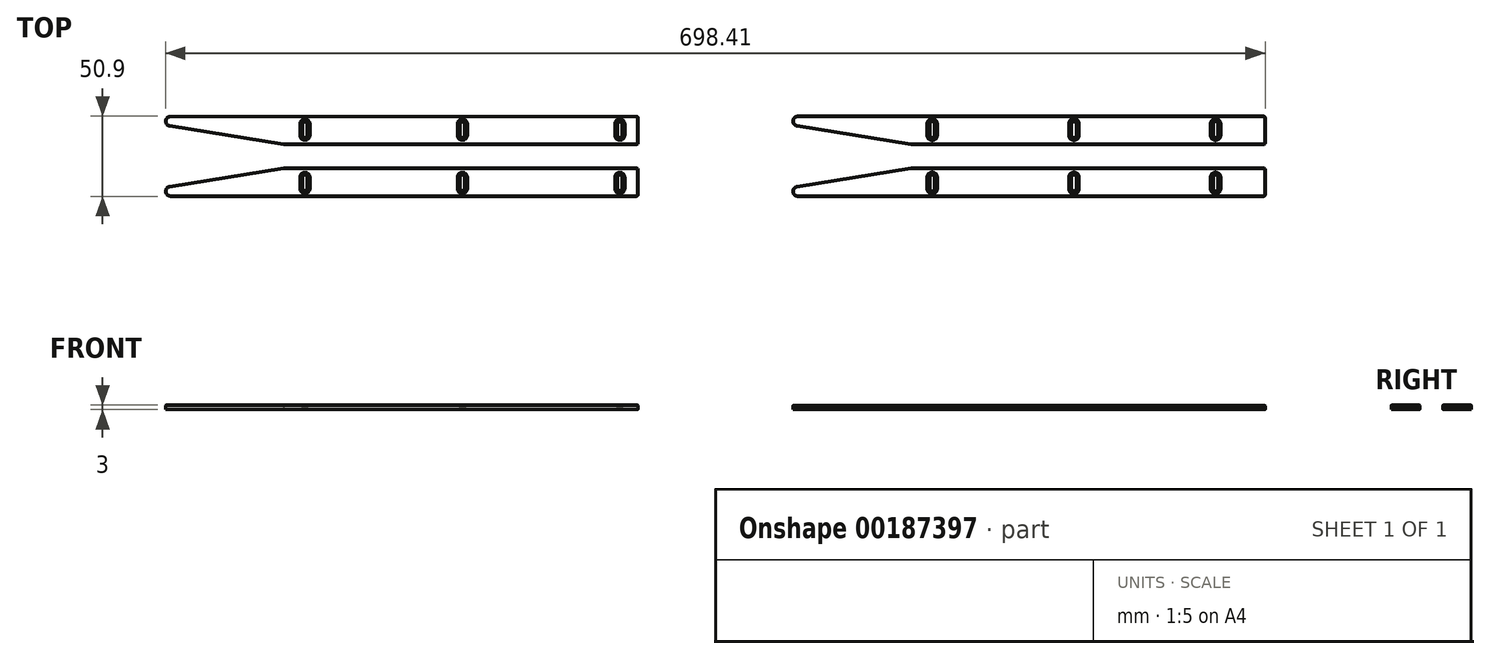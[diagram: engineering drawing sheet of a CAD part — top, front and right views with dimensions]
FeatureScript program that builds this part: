
annotation { "Feature Type Name" : "Feature", "Feature Type Description" : "" }
export const myFeature = defineFeature(function(context is Context, id is Id, definition is map)
    precondition{}
    {
        {
            var Q0;
            Q0=qCreatedBy(makeId("Top.planeOp"),FACE);
            var sketch = newSketch(context, id + "F0", { "sketchPlane" : qUnion([Q0])});
            skLineSegment(sketch, "E0.bottom", {"start": v(0, 0) * mm, "end": v(300, 0) * mm});
            skLineSegment(sketch, "E0.top", {"start": v(0, 18) * mm, "end": v(300, 18) * mm});
            skLineSegment(sketch, "E0.left", {"start": v(0, 0) * mm, "end": v(0, 18) * mm});
            skLineSegment(sketch, "E0.right", {"start": v(300, 0) * mm, "end": v(300, 18) * mm});
            skLineSegment(sketch, "E1.bottom", {"start": v(89.97, 5) * mm, "end": v(86.97, 5) * mm});
            skLineSegment(sketch, "E1.top", {"start": v(89.97, 12) * mm, "end": v(86.97, 12) * mm});
            skLineSegment(sketch, "E1.left", {"start": v(89.97, 5) * mm, "end": v(89.97, 12) * mm});
            skLineSegment(sketch, "E1.right", {"start": v(86.97, 5) * mm, "end": v(86.97, 12) * mm});
            skPoint(sketch, "E1.middle", {"position": v(88.47, 8.5) * mm});
            skLineSegment(sketch, "E2.bottom", {"start": v(189.97, 5) * mm, "end": v(186.97, 5) * mm});
            skLineSegment(sketch, "E2.top", {"start": v(189.97, 12) * mm, "end": v(186.97, 12) * mm});
            skLineSegment(sketch, "E2.left", {"start": v(189.97, 5) * mm, "end": v(189.97, 12) * mm});
            skLineSegment(sketch, "E2.right", {"start": v(186.97, 5) * mm, "end": v(186.97, 12) * mm});
            skPoint(sketch, "E2.middle", {"position": v(188.47, 8.5) * mm});
            skArc(sketch, "E3", {"start": v(86.97, 12) * mm, "mid": v(88.47, 13.5) * mm, "end": v(89.97, 12) * mm});
            skArc(sketch, "E4", {"start": v(186.97, 12) * mm, "mid": v(188.47, 13.5) * mm, "end": v(189.97, 12) * mm});
            skArc(sketch, "E5", {"start": v(86.97, 5) * mm, "mid": v(88.47, 3.5) * mm, "end": v(89.97, 5) * mm});
            skArc(sketch, "E6", {"start": v(186.97, 5) * mm, "mid": v(188.47, 3.5) * mm, "end": v(189.97, 5) * mm});
            skLineSegment(sketch, "E7", {"start": v(0, 5.85) * mm, "end": v(75.04, 18) * mm});
            skLineSegment(sketch, "E8.1.0.0", {"start": v(289.97, 5) * mm, "end": v(286.97, 5) * mm});
            skLineSegment(sketch, "E8.1.0.1", {"start": v(286.97, 5) * mm, "end": v(286.97, 12) * mm});
            skLineSegment(sketch, "E8.1.0.2", {"start": v(289.97, 5) * mm, "end": v(289.97, 12) * mm});
            skLineSegment(sketch, "E8.1.0.3", {"start": v(289.97, 12) * mm, "end": v(286.97, 12) * mm});
            skArc(sketch, "E8.1.0.4", {"start": v(286.97, 5) * mm, "mid": v(288.47, 3.5) * mm, "end": v(289.97, 5) * mm});
            skArc(sketch, "E8.1.0.5", {"start": v(286.97, 12) * mm, "mid": v(288.47, 13.5) * mm, "end": v(289.97, 12) * mm});
            skPoint(sketch, "E8.1.0.6", {"position": v(288.47, 8.5) * mm});
            skLineSegment(sketch, "E8.direction1", {"start": v(186.97, 5) * mm, "end": v(286.97, 5) * mm, "construction": true});
            skSolve(sketch);
        }
        {
            var Q0;
            {var subQ0=sQuery(id+"F0.wireOp",EDGE,"E0.bottom");Q0=makeQuery(id+"F0.imprint","IMPRINT",FACE,{"disambiguationData":[TD([[makeQuery(id+"F0.imprint","IMPRINT",EDGE,{"derivedFrom":subQ0}),1.0]])]});}
            extrude(context, id + "F1", {"entities" : qUnion([Q0]), "depth" : 3 * mm});
        }
        {
            var Q0;
            Q0=makeQuery(id+"F1.opExtrude","SWEPT_FACE",FACE,{"disambiguationData":[OSD([sQuery(id+"F0.wireOp",EDGE,"E0.bottom")])]});
            cPlane(context, id + "F2", {"entities" : qUnion([Q0]), "cplaneType" : CPlaneType.OFFSET, "offset" : 25.4 * mm, "oppositeDirection" : true, "width" : 152.4 * mm, "height" : 152.4 * mm});
        }
        {
            var Q0;
            Q0=makeQuery(id+"F1.opExtrude","SWEPT_BODY",BODY,{"disambiguationData":[OSD([sQuery(id+"F0.wireOp",EDGE,"E0.bottom"),sQuery(id+"F0.wireOp",EDGE,"E0.top"),sQuery(id+"F0.wireOp",EDGE,"E0.left"),sQuery(id+"F0.wireOp",EDGE,"E0.right"),sQuery(id+"F0.wireOp",EDGE,"E1.left"),sQuery(id+"F0.wireOp",EDGE,"E1.right"),sQuery(id+"F0.wireOp",EDGE,"E2.left"),sQuery(id+"F0.wireOp",EDGE,"E2.right"),sQuery(id+"F0.wireOp",EDGE,"E3"),sQuery(id+"F0.wireOp",EDGE,"E4"),sQuery(id+"F0.wireOp",EDGE,"E5"),sQuery(id+"F0.wireOp",EDGE,"E6"),sQuery(id+"F0.wireOp",EDGE,"EhPgQ6kI-HOte-GhGe-7i3y-vseyqDZMkckJ")])]});
            var Q1;
            Q1=qCreatedBy(id+"F2.planeOp",FACE);
            mirror(context, id + "F3", {"entities" : qUnion([Q0]), "mirrorPlane" : qUnion([Q1])});
        }
        {
            var Q0;
            Q0=makeQuery(id+"F1.opExtrude","SWEPT_EDGE",EDGE,{"disambiguationData":[OSD([sQuery(id+"F0.wireOp",EDGE,"E0.left"),sQuery(id+"F0.wireOp",EDGE,"EhPgQ6kI-HOte-GhGe-7i3y-vseyqDZMkckJ")])]});
            fillet(context, id + "F4", {"entities" : qUnion([Q0]), "radius" : 3 * mm, "tangentPropagation" : true, "allowEdgeOverflow" : false});
        }
        {
            var Q0;
            Q0=makeQuery(id+"F3.opPattern","COPY",EDGE,{"derivedFrom":makeQuery(id+"F1.opExtrude","SWEPT_EDGE",EDGE,{"disambiguationData":[OSD([sQuery(id+"F0.wireOp",EDGE,"E0.left"),sQuery(id+"F0.wireOp",EDGE,"EhPgQ6kI-HOte-GhGe-7i3y-vseyqDZMkckJ")])]}),"instanceName":"1"});
            fillet(context, id + "F5", {"entities" : qUnion([Q0]), "radius" : 3 * mm, "tangentPropagation" : true, "allowEdgeOverflow" : false});
        }
        {
            var Q0;
            Q0=makeQuery(id+"F1.opExtrude","SWEPT_EDGE",EDGE,{"disambiguationData":[OSD([sQuery(id+"F0.wireOp",EDGE,"E0.bottom"),sQuery(id+"F0.wireOp",EDGE,"E0.right")])]});
            var Q1;
            Q1=makeQuery(id+"F3.opPattern","COPY",EDGE,{"derivedFrom":makeQuery(id+"F1.opExtrude","SWEPT_EDGE",EDGE,{"disambiguationData":[OSD([sQuery(id+"F0.wireOp",EDGE,"E0.bottom"),sQuery(id+"F0.wireOp",EDGE,"E0.right")])]}),"instanceName":"1"});
            var Q2;
            Q2=makeQuery(id+"F1.opExtrude","SWEPT_EDGE",EDGE,{"disambiguationData":[OSD([sQuery(id+"F0.wireOp",EDGE,"E0.top"),sQuery(id+"F0.wireOp",EDGE,"E0.right")])]});
            var Q3;
            Q3=makeQuery(id+"F3.opPattern","COPY",EDGE,{"derivedFrom":makeQuery(id+"F1.opExtrude","SWEPT_EDGE",EDGE,{"disambiguationData":[OSD([sQuery(id+"F0.wireOp",EDGE,"E0.top"),sQuery(id+"F0.wireOp",EDGE,"E0.right")])]}),"instanceName":"1"});
            fillet(context, id + "F6", {"entities" : qUnion([Q0, Q1, Q2, Q3]), "radius" : 1 * mm, "tangentPropagation" : true, "allowEdgeOverflow" : false});
        }
        {
            var Q0;
            Q0=makeQuery(id+"F1.opExtrude","CAP_EDGE",EDGE,{"disambiguationData":[OSD([sQuery(id+"F0.wireOp",EDGE,"E0.top")])],"isStart":false});
            var Q1;
            Q1=makeQuery(id+"F1.opExtrude","CAP_EDGE",EDGE,{"disambiguationData":[OSD([sQuery(id+"F0.wireOp",EDGE,"EhPgQ6kI-HOte-GhGe-7i3y-vseyqDZMkckJ")])],"isStart":false});
            var Q2;
            Q2=makeQuery(id+"F3.opPattern","COPY",EDGE,{"derivedFrom":makeQuery(id+"F1.opExtrude","CAP_EDGE",EDGE,{"disambiguationData":[OSD([sQuery(id+"F0.wireOp",EDGE,"E0.top")])],"isStart":false}),"instanceName":"1"});
            var Q3;
            Q3=makeQuery(id+"F3.opPattern","COPY",EDGE,{"derivedFrom":makeQuery(id+"F1.opExtrude","CAP_EDGE",EDGE,{"disambiguationData":[OSD([sQuery(id+"F0.wireOp",EDGE,"EhPgQ6kI-HOte-GhGe-7i3y-vseyqDZMkckJ")])],"isStart":false}),"instanceName":"1"});
            chamfer(context, id + "F7", {"entities" : qUnion([Q0, Q1, Q2, Q3]), "width" : .3 * mm, "tangentPropagation" : true});
        }
        {
            var Q0;
            Q0=makeQuery(id+"F1.opExtrude","CAP_EDGE",EDGE,{"disambiguationData":[OSD([sQuery(id+"F0.wireOp",EDGE,"E1.left")])],"isStart":false});
            var Q1;
            Q1=makeQuery(id+"F1.opExtrude","CAP_EDGE",EDGE,{"disambiguationData":[OSD([sQuery(id+"F0.wireOp",EDGE,"E3")])],"isStart":false});
            var Q2;
            Q2=makeQuery(id+"F1.opExtrude","CAP_EDGE",EDGE,{"disambiguationData":[OSD([sQuery(id+"F0.wireOp",EDGE,"E1.right")])],"isStart":false});
            var Q3;
            Q3=makeQuery(id+"F1.opExtrude","CAP_EDGE",EDGE,{"disambiguationData":[OSD([sQuery(id+"F0.wireOp",EDGE,"E5")])],"isStart":false});
            var Q4;
            Q4=makeQuery(id+"F1.opExtrude","CAP_EDGE",EDGE,{"disambiguationData":[OSD([sQuery(id+"F0.wireOp",EDGE,"E4")])],"isStart":false});
            var Q5;
            Q5=makeQuery(id+"F1.opExtrude","CAP_EDGE",EDGE,{"disambiguationData":[OSD([sQuery(id+"F0.wireOp",EDGE,"E2.left")])],"isStart":false});
            var Q6;
            Q6=makeQuery(id+"F1.opExtrude","CAP_EDGE",EDGE,{"disambiguationData":[OSD([sQuery(id+"F0.wireOp",EDGE,"E6")])],"isStart":false});
            var Q7;
            Q7=makeQuery(id+"F1.opExtrude","CAP_EDGE",EDGE,{"disambiguationData":[OSD([sQuery(id+"F0.wireOp",EDGE,"E2.right")])],"isStart":false});
            var Q8;
            Q8=makeQuery(id+"F3.opPattern","COPY",EDGE,{"derivedFrom":makeQuery(id+"F1.opExtrude","CAP_EDGE",EDGE,{"disambiguationData":[OSD([sQuery(id+"F0.wireOp",EDGE,"E2.left")])],"isStart":false}),"instanceName":"1"});
            var Q9;
            Q9=makeQuery(id+"F3.opPattern","COPY",EDGE,{"derivedFrom":makeQuery(id+"F1.opExtrude","CAP_EDGE",EDGE,{"disambiguationData":[OSD([sQuery(id+"F0.wireOp",EDGE,"E4")])],"isStart":false}),"instanceName":"1"});
            var Q10;
            Q10=makeQuery(id+"F3.opPattern","COPY",EDGE,{"derivedFrom":makeQuery(id+"F1.opExtrude","CAP_EDGE",EDGE,{"disambiguationData":[OSD([sQuery(id+"F0.wireOp",EDGE,"E2.right")])],"isStart":false}),"instanceName":"1"});
            var Q11;
            Q11=makeQuery(id+"F3.opPattern","COPY",EDGE,{"derivedFrom":makeQuery(id+"F1.opExtrude","CAP_EDGE",EDGE,{"disambiguationData":[OSD([sQuery(id+"F0.wireOp",EDGE,"E6")])],"isStart":false}),"instanceName":"1"});
            var Q12;
            Q12=makeQuery(id+"F3.opPattern","COPY",EDGE,{"derivedFrom":makeQuery(id+"F1.opExtrude","CAP_EDGE",EDGE,{"disambiguationData":[OSD([sQuery(id+"F0.wireOp",EDGE,"E5")])],"isStart":false}),"instanceName":"1"});
            var Q13;
            Q13=makeQuery(id+"F3.opPattern","COPY",EDGE,{"derivedFrom":makeQuery(id+"F1.opExtrude","CAP_EDGE",EDGE,{"disambiguationData":[OSD([sQuery(id+"F0.wireOp",EDGE,"E1.left")])],"isStart":false}),"instanceName":"1"});
            var Q14;
            Q14=makeQuery(id+"F3.opPattern","COPY",EDGE,{"derivedFrom":makeQuery(id+"F1.opExtrude","CAP_EDGE",EDGE,{"disambiguationData":[OSD([sQuery(id+"F0.wireOp",EDGE,"E3")])],"isStart":false}),"instanceName":"1"});
            var Q15;
            Q15=makeQuery(id+"F3.opPattern","COPY",EDGE,{"derivedFrom":makeQuery(id+"F1.opExtrude","CAP_EDGE",EDGE,{"disambiguationData":[OSD([sQuery(id+"F0.wireOp",EDGE,"E1.right")])],"isStart":false}),"instanceName":"1"});
            var Q16;
            Q16=makeQuery(id+"F1.opExtrude","CAP_EDGE",EDGE,{"disambiguationData":[OSD([sQuery(id+"F0.wireOp",EDGE,"E8.1.0.2")])],"isStart":false});
            var Q17;
            Q17=makeQuery(id+"F1.opExtrude","CAP_EDGE",EDGE,{"disambiguationData":[OSD([sQuery(id+"F0.wireOp",EDGE,"E8.1.0.5")])],"isStart":false});
            var Q18;
            Q18=makeQuery(id+"F1.opExtrude","CAP_EDGE",EDGE,{"disambiguationData":[OSD([sQuery(id+"F0.wireOp",EDGE,"E8.1.0.4")])],"isStart":false});
            var Q19;
            Q19=makeQuery(id+"F1.opExtrude","CAP_EDGE",EDGE,{"disambiguationData":[OSD([sQuery(id+"F0.wireOp",EDGE,"E8.1.0.1")])],"isStart":false});
            var Q20;
            Q20=makeQuery(id+"F3.opPattern","COPY",EDGE,{"derivedFrom":makeQuery(id+"F1.opExtrude","CAP_EDGE",EDGE,{"disambiguationData":[OSD([sQuery(id+"F0.wireOp",EDGE,"E8.1.0.2")])],"isStart":false}),"instanceName":"1"});
            var Q21;
            Q21=makeQuery(id+"F3.opPattern","COPY",EDGE,{"derivedFrom":makeQuery(id+"F1.opExtrude","CAP_EDGE",EDGE,{"disambiguationData":[OSD([sQuery(id+"F0.wireOp",EDGE,"E8.1.0.1")])],"isStart":false}),"instanceName":"1"});
            var Q22;
            Q22=makeQuery(id+"F3.opPattern","COPY",EDGE,{"derivedFrom":makeQuery(id+"F1.opExtrude","CAP_EDGE",EDGE,{"disambiguationData":[OSD([sQuery(id+"F0.wireOp",EDGE,"E8.1.0.4")])],"isStart":false}),"instanceName":"1"});
            var Q23;
            Q23=makeQuery(id+"F3.opPattern","COPY",EDGE,{"derivedFrom":makeQuery(id+"F1.opExtrude","CAP_EDGE",EDGE,{"disambiguationData":[OSD([sQuery(id+"F0.wireOp",EDGE,"E8.1.0.5")])],"isStart":false}),"instanceName":"1"});
            chamfer(context, id + "F8", {"entities" : qUnion([Q0, Q1, Q2, Q3, Q4, Q5, Q6, Q7, Q8, Q9, Q10, Q11, Q12, Q13, Q14, Q15, Q16, Q17, Q18, Q19, Q20, Q21, Q22, Q23]), "chamferType" : ChamferType.OFFSET_ANGLE, "width" : 1.7 * mm, "oppositeDirection" : false, "angle" : 45 * degree, "tangentPropagation" : true});
        }
        {
            var Q0;
            Q0=makeQuery(id+"F1.opExtrude","CAP_FACE",FACE,{"disambiguationData":[OSD([sQuery(id+"F0.wireOp",EDGE,"E0.bottom"),sQuery(id+"F0.wireOp",EDGE,"E0.top"),sQuery(id+"F0.wireOp",EDGE,"E0.left"),sQuery(id+"F0.wireOp",EDGE,"E0.right"),sQuery(id+"F0.wireOp",EDGE,"E1.left"),sQuery(id+"F0.wireOp",EDGE,"E1.right"),sQuery(id+"F0.wireOp",EDGE,"E2.left"),sQuery(id+"F0.wireOp",EDGE,"E2.right"),sQuery(id+"F0.wireOp",EDGE,"E3"),sQuery(id+"F0.wireOp",EDGE,"E4"),sQuery(id+"F0.wireOp",EDGE,"E5"),sQuery(id+"F0.wireOp",EDGE,"E6"),sQuery(id+"F0.wireOp",EDGE,"E7"),sQuery(id+"F0.wireOp",EDGE,"E8.1.0.1"),sQuery(id+"F0.wireOp",EDGE,"E8.1.0.2"),sQuery(id+"F0.wireOp",EDGE,"E8.1.0.4"),sQuery(id+"F0.wireOp",EDGE,"E8.1.0.5")])],"isStart":true});
            var sketch = newSketch(context, id + "F9", { "sketchPlane" : qUnion([Q0])});
            skLineSegment(sketch, "E9.bottom", {"start": v(398.4, -50.85) * mm, "end": v(698.4, -50.85) * mm});
            skLineSegment(sketch, "E9.top", {"start": v(398.4, -32.85) * mm, "end": v(698.4, -32.85) * mm});
            skLineSegment(sketch, "E9.left", {"start": v(398.4, -50.85) * mm, "end": v(398.4, -32.85) * mm});
            skLineSegment(sketch, "E9.right", {"start": v(698.4, -50.85) * mm, "end": v(698.4, -32.85) * mm});
            skLineSegment(sketch, "E10.bottom", {"start": v(488.38, -45.85) * mm, "end": v(485.38, -45.85) * mm});
            skLineSegment(sketch, "E10.top", {"start": v(488.38, -38.85) * mm, "end": v(485.38, -38.85) * mm});
            skLineSegment(sketch, "E10.left", {"start": v(488.38, -45.85) * mm, "end": v(488.38, -38.85) * mm});
            skLineSegment(sketch, "E10.right", {"start": v(485.38, -45.85) * mm, "end": v(485.38, -38.85) * mm});
            skPoint(sketch, "E10.middle", {"position": v(486.88, -42.35) * mm});
            skLineSegment(sketch, "E11.bottom", {"start": v(578.38, -45.85) * mm, "end": v(575.38, -45.85) * mm});
            skLineSegment(sketch, "E11.top", {"start": v(578.38, -38.85) * mm, "end": v(575.38, -38.85) * mm});
            skLineSegment(sketch, "E11.left", {"start": v(578.38, -45.85) * mm, "end": v(578.38, -38.85) * mm});
            skLineSegment(sketch, "E11.right", {"start": v(575.38, -45.85) * mm, "end": v(575.38, -38.85) * mm});
            skPoint(sketch, "E11.middle", {"position": v(576.88, -42.35) * mm});
            skArc(sketch, "E12", {"start": v(485.38, -38.85) * mm, "mid": v(486.88, -37.35) * mm, "end": v(488.38, -38.85) * mm});
            skArc(sketch, "E13", {"start": v(575.38, -38.85) * mm, "mid": v(576.88, -37.35) * mm, "end": v(578.38, -38.85) * mm});
            skArc(sketch, "E14", {"start": v(485.38, -45.85) * mm, "mid": v(486.88, -47.35) * mm, "end": v(488.38, -45.85) * mm});
            skArc(sketch, "E15", {"start": v(575.38, -45.85) * mm, "mid": v(576.88, -47.35) * mm, "end": v(578.38, -45.85) * mm});
            skLineSegment(sketch, "E16", {"start": v(398.4, -45) * mm, "end": v(473.44, -32.85) * mm});
            skLineSegment(sketch, "E17.1.0.0", {"start": v(668.38, -45.85) * mm, "end": v(665.38, -45.85) * mm});
            skLineSegment(sketch, "E17.1.0.1", {"start": v(665.38, -45.85) * mm, "end": v(665.38, -38.85) * mm});
            skLineSegment(sketch, "E17.1.0.2", {"start": v(668.38, -45.85) * mm, "end": v(668.38, -38.85) * mm});
            skLineSegment(sketch, "E17.1.0.3", {"start": v(668.38, -38.85) * mm, "end": v(665.38, -38.85) * mm});
            skArc(sketch, "E17.1.0.4", {"start": v(665.38, -45.85) * mm, "mid": v(666.88, -47.35) * mm, "end": v(668.38, -45.85) * mm});
            skArc(sketch, "E17.1.0.5", {"start": v(665.38, -38.85) * mm, "mid": v(666.88, -37.35) * mm, "end": v(668.38, -38.85) * mm});
            skPoint(sketch, "E17.1.0.6", {"position": v(666.88, -42.35) * mm});
            skLineSegment(sketch, "E17.direction1", {"start": v(575.38, -45.85) * mm, "end": v(665.38, -45.85) * mm, "construction": true});
            skSolve(sketch);
        }
        {
            var Q0;
            {var subQ1=sQuery(id+"F9.wireOp",EDGE,"E9.bottom");Q0=makeQuery(id+"F9.imprint","IMPRINT",FACE,{"disambiguationData":[TD([[makeQuery(id+"F9.imprint","IMPRINT",EDGE,{"derivedFrom":subQ1}),1.0]])]});}
            extrude(context, id + "F10", {"entities" : qUnion([Q0]), "oppositeDirection" : true, "depth" : 2.7 * mm});
        }
        {
            var Q0;
            Q0=makeQuery(id+"F10.opExtrude","SWEPT_EDGE",EDGE,{"disambiguationData":[OSD([sQuery(id+"F9.wireOp",EDGE,"E9.left"),sQuery(id+"F9.wireOp",EDGE,"E16")])]});
            var Q1;
            Q1=makeQuery(id+"F10.opExtrude","SWEPT_EDGE",EDGE,{"disambiguationData":[OSD([sQuery(id+"F9.wireOp",EDGE,"E9.bottom"),sQuery(id+"F9.wireOp",EDGE,"E9.left")])]});
            fillet(context, id + "F11", {"entities" : qUnion([Q0, Q1]), "radius" : 3 * mm, "tangentPropagation" : true, "allowEdgeOverflow" : false});
        }
        {
            var Q0;
            Q0=makeQuery(id+"F10.opExtrude","CAP_EDGE",EDGE,{"disambiguationData":[OSD([sQuery(id+"F9.wireOp",EDGE,"E14")])],"isStart":false});
            var Q1;
            Q1=makeQuery(id+"F10.opExtrude","CAP_EDGE",EDGE,{"disambiguationData":[OSD([sQuery(id+"F9.wireOp",EDGE,"E10.right")])],"isStart":false});
            var Q2;
            Q2=makeQuery(id+"F10.opExtrude","CAP_EDGE",EDGE,{"disambiguationData":[OSD([sQuery(id+"F9.wireOp",EDGE,"E10.left")])],"isStart":false});
            var Q3;
            Q3=makeQuery(id+"F10.opExtrude","CAP_EDGE",EDGE,{"disambiguationData":[OSD([sQuery(id+"F9.wireOp",EDGE,"E12")])],"isStart":false});
            var Q4;
            Q4=makeQuery(id+"F10.opExtrude","CAP_EDGE",EDGE,{"disambiguationData":[OSD([sQuery(id+"F9.wireOp",EDGE,"E11.right")])],"isStart":false});
            var Q5;
            Q5=makeQuery(id+"F10.opExtrude","CAP_EDGE",EDGE,{"disambiguationData":[OSD([sQuery(id+"F9.wireOp",EDGE,"E15")])],"isStart":false});
            var Q6;
            Q6=makeQuery(id+"F10.opExtrude","CAP_EDGE",EDGE,{"disambiguationData":[OSD([sQuery(id+"F9.wireOp",EDGE,"E11.left")])],"isStart":false});
            var Q7;
            Q7=makeQuery(id+"F10.opExtrude","CAP_EDGE",EDGE,{"disambiguationData":[OSD([sQuery(id+"F9.wireOp",EDGE,"E13")])],"isStart":false});
            var Q8;
            Q8=makeQuery(id+"F10.opExtrude","CAP_EDGE",EDGE,{"disambiguationData":[OSD([sQuery(id+"F9.wireOp",EDGE,"E17.1.0.1")])],"isStart":false});
            var Q9;
            Q9=makeQuery(id+"F10.opExtrude","CAP_EDGE",EDGE,{"disambiguationData":[OSD([sQuery(id+"F9.wireOp",EDGE,"E17.1.0.2")])],"isStart":false});
            var Q10;
            Q10=makeQuery(id+"F10.opExtrude","CAP_EDGE",EDGE,{"disambiguationData":[OSD([sQuery(id+"F9.wireOp",EDGE,"E17.1.0.4")])],"isStart":false});
            var Q11;
            Q11=makeQuery(id+"F10.opExtrude","CAP_EDGE",EDGE,{"disambiguationData":[OSD([sQuery(id+"F9.wireOp",EDGE,"E17.1.0.5")])],"isStart":false});
            chamfer(context, id + "F12", {"entities" : qUnion([Q0, Q1, Q2, Q3, Q4, Q5, Q6, Q7, Q8, Q9, Q10, Q11]), "chamferType" : ChamferType.OFFSET_ANGLE, "width" : 1.7 * mm, "oppositeDirection" : false, "angle" : 45 * degree, "tangentPropagation" : true});
        }
        {
            var Q0;
            Q0=makeQuery(id+"F10.opExtrude","SWEPT_EDGE",EDGE,{"disambiguationData":[OSD([sQuery(id+"F9.wireOp",EDGE,"E9.top"),sQuery(id+"F9.wireOp",EDGE,"E9.right")])]});
            var Q1;
            Q1=makeQuery(id+"F10.opExtrude","SWEPT_EDGE",EDGE,{"disambiguationData":[OSD([sQuery(id+"F9.wireOp",EDGE,"E9.bottom"),sQuery(id+"F9.wireOp",EDGE,"E9.right")])]});
            fillet(context, id + "F13", {"entities" : qUnion([Q0, Q1]), "radius" : 1 * mm, "tangentPropagation" : true, "allowEdgeOverflow" : false});
        }
        {
            var Q0;
            Q0=makeQuery(id+"F10.opExtrude","CAP_FACE",FACE,{"disambiguationData":[OSD([sQuery(id+"F9.wireOp",EDGE,"E9.bottom"),sQuery(id+"F9.wireOp",EDGE,"E9.top"),sQuery(id+"F9.wireOp",EDGE,"E9.left"),sQuery(id+"F9.wireOp",EDGE,"E9.right"),sQuery(id+"F9.wireOp",EDGE,"E10.left"),sQuery(id+"F9.wireOp",EDGE,"E10.right"),sQuery(id+"F9.wireOp",EDGE,"E11.left"),sQuery(id+"F9.wireOp",EDGE,"E11.right"),sQuery(id+"F9.wireOp",EDGE,"E12"),sQuery(id+"F9.wireOp",EDGE,"E13"),sQuery(id+"F9.wireOp",EDGE,"E14"),sQuery(id+"F9.wireOp",EDGE,"E15"),sQuery(id+"F9.wireOp",EDGE,"E16"),sQuery(id+"F9.wireOp",EDGE,"E17.1.0.1"),sQuery(id+"F9.wireOp",EDGE,"E17.1.0.2"),sQuery(id+"F9.wireOp",EDGE,"E17.1.0.4"),sQuery(id+"F9.wireOp",EDGE,"E17.1.0.5")])],"isStart":false});
            chamfer(context, id + "F14", {"entities" : qUnion([Q0]), "width" : .3 * mm, "tangentPropagation" : true});
        }
        {
            var Q0;
            Q0=makeQuery(id+"F10.opExtrude","SWEPT_BODY",BODY,{"disambiguationData":[OSD([sQuery(id+"F9.wireOp",EDGE,"E9.bottom"),sQuery(id+"F9.wireOp",EDGE,"E9.top"),sQuery(id+"F9.wireOp",EDGE,"E9.left"),sQuery(id+"F9.wireOp",EDGE,"E9.right"),sQuery(id+"F9.wireOp",EDGE,"E10.left"),sQuery(id+"F9.wireOp",EDGE,"E10.right"),sQuery(id+"F9.wireOp",EDGE,"E11.left"),sQuery(id+"F9.wireOp",EDGE,"E11.right"),sQuery(id+"F9.wireOp",EDGE,"E12"),sQuery(id+"F9.wireOp",EDGE,"E13"),sQuery(id+"F9.wireOp",EDGE,"E14"),sQuery(id+"F9.wireOp",EDGE,"E15"),sQuery(id+"F9.wireOp",EDGE,"E16"),sQuery(id+"F9.wireOp",EDGE,"E17.1.0.1"),sQuery(id+"F9.wireOp",EDGE,"E17.1.0.2"),sQuery(id+"F9.wireOp",EDGE,"E17.1.0.4"),sQuery(id+"F9.wireOp",EDGE,"E17.1.0.5")])]});
            var Q1;
            Q1=qCreatedBy(id+"F2.planeOp",FACE);
            mirror(context, id + "F15", {"entities" : qUnion([Q0]), "mirrorPlane" : qUnion([Q1])});
        }
    });
